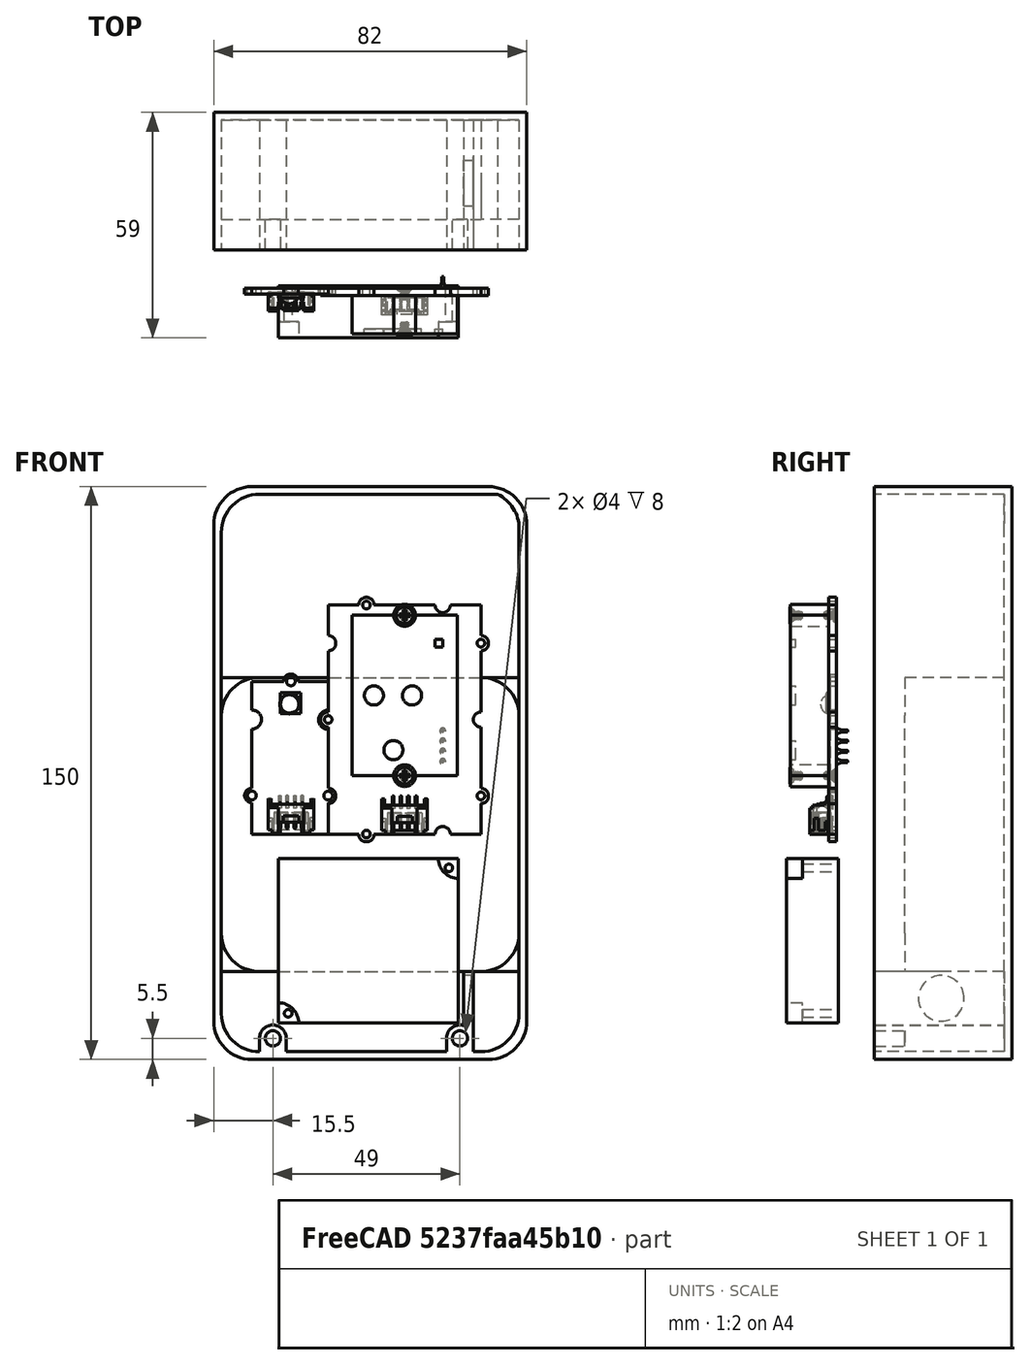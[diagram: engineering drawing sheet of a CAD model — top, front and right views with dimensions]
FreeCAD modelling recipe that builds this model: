
FCSTD DOCUMENT  (FreeCAD 0.20R29177 +233 (Git))
Label: wearableCad2022
License: All rights reserved
LicenseURL: http://en.wikipedia.org/wiki/All_rights_reserved
objects: Part::Cylinder×26, Part::Box×23, Part::Cut×22, Part::MultiFuse×11, Part::Feature×3
note: 85 computed .brp shape members not serialized (recipe doc carries the construction recipe); baked Part::Feature solids carry a one-line shape summary decoded from their .brp

FEATURE [Part::Feature] Feature  label="Odroid-C4"
  Placement = pos=(66,-10,0) rot=(0.57735,-0.57735,0.57735;2.0944rad)
  shape: bbox 57.1 x 20.65 x 89.5 mm, 2775 faces, 0 solids (baked)
FEATURE [Part::Feature] Feature001  label="SCD30"
  Placement = pos=(-1.3e-14,-22,57) rot=(0,-1,0;1.5708rad)
  shape: bbox 44 x 15.1 x 64 mm, 422 faces, 13 solids (baked)
FEATURE [Part::Feature] Feature002  label="bme280"
  Placement = pos=(-60,-20,58) rot=(0.707107,0,0.707107;3.14159rad)
  shape: bbox 23.8 x 6.016 x 41.9 mm, 221 faces, 2 solids (baked)
FEATURE [Part::MultiFuse] Fusion  label="i2cSensors"
  Placement = pos=(68,0,0) rot=(0,0,1;0rad)
  Shapes = -> [Feature001,Feature002]
FEATURE [Part::Box] Box  label="ips7100"
  AttacherType = Attacher::AttachEngine3D
  Height = 43.1
  Length = 47.1
  Width = 13.55
FEATURE [Part::Cylinder] Cylinder
  Angle = 360
  AttacherType = Attacher::AttachEngine3D
  FirstAngle = 0
  Height = 13.55
  Placement = pos=(2.5,13.55,2.5) rot=(1,0,0;1.5708rad)
  Radius = 1
  SecondAngle = 0
FEATURE [Part::Cylinder] Cylinder001  label="semiCut"
  Angle = 90
  AttacherType = Attacher::AttachEngine3D
  FirstAngle = 0
  Height = 4.13
  Placement = pos=(0,4.13,-9e-16) rot=(1,0,0;1.5708rad)
  Radius = 5.25
  SecondAngle = 0
FEATURE [Part::MultiFuse] Fusion001  label="ipsCut"
  Shapes = -> [Cylinder,Cylinder001]
FEATURE [Part::Cylinder] Cylinder002
  Angle = 360
  AttacherType = Attacher::AttachEngine3D
  FirstAngle = 0
  Height = 13.55
  Placement = pos=(2.5,13.55,2.5) rot=(1,0,0;1.5708rad)
  Radius = 1
  SecondAngle = 0
FEATURE [Part::Cylinder] Cylinder003  label="semiCut001"
  Angle = 90
  AttacherType = Attacher::AttachEngine3D
  FirstAngle = 0
  Height = 4.13
  Placement = pos=(0,4.13,-9e-16) rot=(1,0,0;1.5708rad)
  Radius = 5.25
  SecondAngle = 0
FEATURE [Part::MultiFuse] Fusion002  label="ipsCut001"
  Placement = pos=(47.1,0,43.1) rot=(0,1,0;3.14159rad)
  Shapes = -> [Cylinder002,Cylinder003]
FEATURE [Part::MultiFuse] Fusion003
  Shapes = -> [Fusion001,Fusion002]
FEATURE [Part::Cut] Cut  label="ips7100V"
  Base = -> Box
  Placement = pos=(15,-33,7.55) rot=(0,0,1;0rad)
  Tool = -> Fusion003
FEATURE [Part::Box] Box001  label="V25B"
  AttacherType = Attacher::AttachEngine3D
  Height = 77
  Length = 78
  Width = 26
FEATURE [Part::Cylinder] Cylinder004
  Angle = 90
  AttacherType = Attacher::AttachEngine3D
  FirstAngle = 0
  Height = 26
  Placement = pos=(0,26,-5.8e-15) rot=(1,0,0;1.5708rad)
  Radius = 10
  SecondAngle = 0
FEATURE [Part::Box] Box002  label="Cube"
  AttacherType = Attacher::AttachEngine3D
  Height = 10
  Length = 10
  Width = 26
FEATURE [Part::Cut] Cut001
  Base = -> Box002
  Placement = pos=(68,0,67) rot=(0,0,1;0rad)
  Tool = -> Cylinder004
FEATURE [Part::Box] Box003  label="Cube001"
  AttacherType = Attacher::AttachEngine3D
  Height = 10
  Length = 10
  Width = 26
FEATURE [Part::Cylinder] Cylinder005
  Angle = 90
  AttacherType = Attacher::AttachEngine3D
  FirstAngle = 0
  Height = 26
  Placement = pos=(0,26,-5.8e-15) rot=(1,0,0;1.5708rad)
  Radius = 10
  SecondAngle = 0
FEATURE [Part::Cut] Cut002
  Base = -> Box003
  Placement = pos=(68,0,10) rot=(0,1,0;1.5708rad)
  Tool = -> Cylinder005
FEATURE [Part::Box] Box004  label="Cube002"
  AttacherType = Attacher::AttachEngine3D
  Height = 10
  Length = 10
  Width = 26
FEATURE [Part::Cylinder] Cylinder006
  Angle = 90
  AttacherType = Attacher::AttachEngine3D
  FirstAngle = 0
  Height = 26
  Placement = pos=(0,26,-5.8e-15) rot=(1,0,0;1.5708rad)
  Radius = 10
  SecondAngle = 0
FEATURE [Part::Cut] Cut003
  Base = -> Box004
  Placement = pos=(10,0,10) rot=(0,1,0;3.14159rad)
  Tool = -> Cylinder006
FEATURE [Part::Box] Box005  label="Cube003"
  AttacherType = Attacher::AttachEngine3D
  Height = 10
  Length = 10
  Width = 26
FEATURE [Part::Cylinder] Cylinder007
  Angle = 90
  AttacherType = Attacher::AttachEngine3D
  FirstAngle = 0
  Height = 26
  Placement = pos=(0,26,-5.8e-15) rot=(1,0,0;1.5708rad)
  Radius = 10
  SecondAngle = 0
FEATURE [Part::Cut] Cut004
  Base = -> Box005
  Placement = pos=(10,0,67) rot=(0,-1,0;1.5708rad)
  Tool = -> Cylinder007
FEATURE [Part::MultiFuse] Fusion004  label="v25Cuts"
  Shapes = -> [Cut001,Cut002,Cut003,Cut004]
FEATURE [Part::Cut] Cut005  label="V25B001"
  Base = -> Box001
  Placement = pos=(0,-2,21) rot=(0,0,1;0rad)
  Tool = -> Fusion004
FEATURE [Part::Box] Box007  label="Cube004"
  AttacherType = Attacher::AttachEngine3D
  Height = 10
  Length = 10
  Placement = pos=(0,-10,0) rot=(0,0,1;0rad)
  Width = 36
FEATURE [Part::Cylinder] Cylinder008
  Angle = 90
  AttacherType = Attacher::AttachEngine3D
  FirstAngle = 0
  Height = 36
  Placement = pos=(0,26,-5.8e-15) rot=(1,0,0;1.5708rad)
  Radius = 10
  SecondAngle = 0
FEATURE [Part::Cut] Cut006
  Base = -> Box007
  Placement = pos=(8,18,8) rot=(-0.707107,0,0.707107;3.14159rad)
  Tool = -> Cylinder008
FEATURE [Part::Box] Box008  label="baseOut001"
  AttacherType = Attacher::AttachEngine3D
  Height = 150
  Length = 82
  Placement = pos=(80,26,-2) rot=(0,0,1;3.14159rad)
  Width = 36
FEATURE [Part::Box] Box009  label="Cube005"
  AttacherType = Attacher::AttachEngine3D
  Height = 10
  Length = 10
  Placement = pos=(0,-10,0) rot=(0,0,1;0rad)
  Width = 36
FEATURE [Part::Cylinder] Cylinder009
  Angle = 90
  AttacherType = Attacher::AttachEngine3D
  FirstAngle = 0
  Height = 36
  Placement = pos=(0,26,-5.8e-15) rot=(1,0,0;1.5708rad)
  Radius = 10
  SecondAngle = 0
FEATURE [Part::Cut] Cut007
  Base = -> Box009
  Placement = pos=(70,18,8) rot=(1,0,0;3.14159rad)
  Tool = -> Cylinder009
FEATURE [Part::Box] Box010  label="Cube006"
  AttacherType = Attacher::AttachEngine3D
  Height = 10
  Length = 10
  Placement = pos=(0,-10,0) rot=(0,0,1;0rad)
  Width = 36
FEATURE [Part::Cylinder] Cylinder010
  Angle = 90
  AttacherType = Attacher::AttachEngine3D
  FirstAngle = 0
  Height = 36
  Placement = pos=(0,26,-5.8e-15) rot=(1,0,0;1.5708rad)
  Radius = 10
  SecondAngle = 0
FEATURE [Part::Cut] Cut008
  Base = -> Box010
  Placement = pos=(8,18,138) rot=(0,0,1;3.14159rad)
  Tool = -> Cylinder010
FEATURE [Part::Box] Box011  label="Cube007"
  AttacherType = Attacher::AttachEngine3D
  Height = 10
  Length = 10
  Placement = pos=(0,-10,0) rot=(0,0,1;0rad)
  Width = 36
FEATURE [Part::Cylinder] Cylinder011
  Angle = 90
  AttacherType = Attacher::AttachEngine3D
  FirstAngle = 0
  Height = 36
  Placement = pos=(0,26,-5.8e-15) rot=(1,0,0;1.5708rad)
  Radius = 10
  SecondAngle = 0
FEATURE [Part::Cut] Cut009
  Base = -> Box011
  Placement = pos=(70,18,138) rot=(0.707107,0,0.707107;3.14159rad)
  Tool = -> Cylinder011
FEATURE [Part::MultiFuse] Fusion005
  Placement = pos=(0,-2,0) rot=(0,0,1;0rad)
  Shapes = -> [Cut006,Cut007,Cut008,Cut009]
FEATURE [Part::Cut] Cut010  label="BaseOut"
  Base = -> Box008
  Tool = -> Fusion005
FEATURE [Part::Box] Box013  label="Cube009"
  AttacherType = Attacher::AttachEngine3D
  Height = 10
  Length = 10
  Placement = pos=(0,-8,0) rot=(0,0,1;0rad)
  Width = 34
FEATURE [Part::Box] Box014  label="baseOut002"
  AttacherType = Attacher::AttachEngine3D
  Height = 146
  Length = 78
  Placement = pos=(80,26,-2) rot=(0,0,1;3.14159rad)
  Width = 34
FEATURE [Part::Box] Box015  label="Cube010"
  AttacherType = Attacher::AttachEngine3D
  Height = 10
  Length = 10
  Placement = pos=(0,-8,0) rot=(0,0,1;0rad)
  Width = 34
FEATURE [Part::Box] Box016  label="Cube011"
  AttacherType = Attacher::AttachEngine3D
  Height = 10
  Length = 10
  Placement = pos=(0,-8,0) rot=(0,0,1;0rad)
  Width = 34
FEATURE [Part::Box] Box017  label="Cube012"
  AttacherType = Attacher::AttachEngine3D
  Height = 10
  Length = 10
  Placement = pos=(0,-8,0) rot=(0,0,1;0rad)
  Width = 34
FEATURE [Part::Cylinder] Cylinder013
  Angle = 90
  AttacherType = Attacher::AttachEngine3D
  FirstAngle = 0
  Height = 34
  Placement = pos=(0,26,-5.8e-15) rot=(1,0,0;1.5708rad)
  Radius = 10
  SecondAngle = 0
FEATURE [Part::Cut] Cut012
  Base = -> Box013
  Placement = pos=(12,18,8) rot=(0.707107,0,-0.707107;3.14159rad)
  Tool = -> Cylinder013
FEATURE [Part::Cylinder] Cylinder014
  Angle = 90
  AttacherType = Attacher::AttachEngine3D
  FirstAngle = 0
  Height = 34
  Placement = pos=(0,26,-5.8e-15) rot=(1,0,0;1.5708rad)
  Radius = 10
  SecondAngle = 0
FEATURE [Part::Cut] Cut013
  Base = -> Box015
  Placement = pos=(70,18,8) rot=(1,0,0;3.14159rad)
  Tool = -> Cylinder014
FEATURE [Part::Cylinder] Cylinder015
  Angle = 90
  AttacherType = Attacher::AttachEngine3D
  FirstAngle = 0
  Height = 34
  Placement = pos=(0,26,-5.8e-15) rot=(1,0,0;1.5708rad)
  Radius = 10
  SecondAngle = 0
FEATURE [Part::Cut] Cut014
  Base = -> Box016
  Placement = pos=(12,18,134) rot=(0,0,1;3.14159rad)
  Tool = -> Cylinder015
FEATURE [Part::Cylinder] Cylinder016
  Angle = 90
  AttacherType = Attacher::AttachEngine3D
  FirstAngle = 0
  Height = 34
  Placement = pos=(0,26,-5.8e-15) rot=(1,0,0;1.5708rad)
  Radius = 10
  SecondAngle = 0
FEATURE [Part::Cut] Cut015
  Base = -> Box017
  Placement = pos=(70,18,135) rot=(0.707107,0,0.707107;3.14159rad)
  Tool = -> Cylinder016
FEATURE [Part::MultiFuse] Fusion006
  Shapes = -> [Cut012,Cut013,Cut014,Cut015]
FEATURE [Part::Cut] Cut016  label="BaseOut001"
  Base = -> Box014
  Placement = pos=(-2,-2,2) rot=(0,0,1;0rad)
  Tool = -> Fusion006
FEATURE [Part::Cut] Cut017  label="baseOut"
  Base = -> Cut010
  Tool = -> Cut016
FEATURE [Part::Box] Box018  label="Cube013"
  AttacherType = Attacher::AttachEngine3D
  Height = 10
  Length = 10
  Placement = pos=(10,26,0) rot=(0,0,-1;3.14159rad)
  Width = 26
FEATURE [Part::Cylinder] Cylinder017
  Angle = 90
  AttacherType = Attacher::AttachEngine3D
  FirstAngle = 0
  Height = 26
  Placement = pos=(0,26,-5.8e-15) rot=(1,0,0;1.5708rad)
  Radius = 10
  SecondAngle = 0
FEATURE [Part::Cut] Cut018  label="batterySupport"
  Base = -> Box018
  Placement = pos=(10,-2,31) rot=(0,1,0;3.14159rad)
  Tool = -> Cylinder017
FEATURE [Part::Box] Box019  label="Cube014"
  AttacherType = Attacher::AttachEngine3D
  Height = 10
  Length = 10
  Placement = pos=(10,26,0) rot=(0,0,1;3.14159rad)
  Width = 26
FEATURE [Part::Cylinder] Cylinder018
  Angle = 90
  AttacherType = Attacher::AttachEngine3D
  FirstAngle = 0
  Height = 26
  Placement = pos=(0,26,-5.8e-15) rot=(1,0,0;1.5708rad)
  Radius = 10
  SecondAngle = 0
FEATURE [Part::Cut] Cut019  label="batterySupport001"
  Base = -> Box019
  Placement = pos=(68,-2,31) rot=(0,-1,0;4.71239rad)
  Tool = -> Cylinder018
FEATURE [Part::Box] Box020  label="Cube015"
  AttacherType = Attacher::AttachEngine3D
  Height = 10
  Length = 10
  Placement = pos=(10,26,0) rot=(0,0,1;3.14159rad)
  Width = 26
FEATURE [Part::Cylinder] Cylinder019
  Angle = 90
  AttacherType = Attacher::AttachEngine3D
  FirstAngle = 0
  Height = 26
  Placement = pos=(0,26,-5.8e-15) rot=(1,0,0;1.5708rad)
  Radius = 10
  SecondAngle = 0
FEATURE [Part::Cut] Cut020  label="batterySupport002"
  Base = -> Box020
  Placement = pos=(68,-2,88) rot=(0,0,1;0rad)
  Tool = -> Cylinder019
FEATURE [Part::Box] Box021  label="Cube016"
  AttacherType = Attacher::AttachEngine3D
  Height = 10
  Length = 10
  Placement = pos=(10,26,0) rot=(0,0,1;3.14159rad)
  Width = 26
FEATURE [Part::Cylinder] Cylinder020
  Angle = 90
  AttacherType = Attacher::AttachEngine3D
  FirstAngle = 0
  Height = 26
  Placement = pos=(0,26,-5.8e-15) rot=(1,0,0;1.5708rad)
  Radius = 10
  SecondAngle = 0
FEATURE [Part::Cut] Cut021  label="batterySupport003"
  Base = -> Box021
  Placement = pos=(10,-2,88) rot=(0,1,0;4.71239rad)
  Tool = -> Cylinder020
FEATURE [Part::Cylinder] Cylinder021
  Angle = 360
  AttacherType = Attacher::AttachEngine3D
  FirstAngle = 0
  Height = 34
  Placement = pos=(13.5,24,3.5) rot=(1,0,0;1.5708rad)
  Radius = 3.5
  SecondAngle = 0
FEATURE [Part::Cylinder] Cylinder022
  Angle = 360
  AttacherType = Attacher::AttachEngine3D
  FirstAngle = 0
  Height = 8
  Placement = pos=(13.5,-2,3.5) rot=(1,0,0;1.5708rad)
  Radius = 2
  SecondAngle = 0
FEATURE [Part::Box] Box022  label="Cube017"
  AttacherType = Attacher::AttachEngine3D
  Height = 3.5
  Length = 7
  Placement = pos=(10,24,3.5) rot=(1,0,0;3.14159rad)
  Width = 34
FEATURE [Part::Cylinder] Cylinder023
  Angle = 360
  AttacherType = Attacher::AttachEngine3D
  FirstAngle = 0
  Height = 34
  Placement = pos=(62.5,24,3.5) rot=(1,0,0;1.5708rad)
  Radius = 3.5
  SecondAngle = 0
FEATURE [Part::Cylinder] Cylinder024
  Angle = 360
  AttacherType = Attacher::AttachEngine3D
  FirstAngle = 0
  Height = 8
  Placement = pos=(62.5,-2,3.5) rot=(1,0,0;1.5708rad)
  Radius = 2
  SecondAngle = 0
FEATURE [Part::Box] Box023  label="Cube018"
  AttacherType = Attacher::AttachEngine3D
  Height = 3.5
  Length = 7
  Placement = pos=(59,24,3.5) rot=(1,0,0;3.14159rad)
  Width = 34
FEATURE [Part::Cylinder] Cylinder025
  Angle = 360
  AttacherType = Attacher::AttachEngine3D
  FirstAngle = 0
  Height = 20
  Radius = 6
  SecondAngle = 0
FEATURE [Part::Cylinder] Cylinder026
  Angle = 360
  AttacherType = Attacher::AttachEngine3D
  FirstAngle = 0
  Height = 5
  Radius = 7
  SecondAngle = 0
FEATURE [Part::MultiFuse] Fusion007  label="powerSwitch"
  Placement = pos=(71,7.5,14) rot=(0,1,0;4.71239rad)
  Shapes = -> [Cylinder025,Cylinder026]
FEATURE [Part::Box] Box024  label="Cube019"
  AttacherType = Attacher::AttachEngine3D
  Height = 17.5
  Length = 2.5
  Placement = pos=(63.5,24,21) rot=(1,0,0;3.14159rad)
  Width = 34
FEATURE [Part::MultiFuse] Fusion008  label="base"
  Shapes = -> [Cut017,Cut018,Cut019,Cut020,Cut021]
FEATURE [Part::MultiFuse] Fusion009  label="base001"
  Shapes = -> [Cylinder021,Cylinder023,Box022,Box023,Box024,Fusion008]
FEATURE [Part::MultiFuse] Fusion010  label="baseCuts"
  Shapes = -> [Cylinder024,Cylinder022,Fusion007]
FEATURE [Part::Cut] Cut022  label="baseCuts001"
  Base = -> Fusion009
  Tool = -> Fusion010
